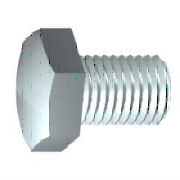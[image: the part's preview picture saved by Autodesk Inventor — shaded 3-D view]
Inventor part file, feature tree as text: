
AUTODESK INVENTOR PART (.ipt)
format: ipt  version: 2023 (Build 270158000, 158)  size: 218,112 bytes
history: native  units: mm
features: sketch x4, other x2, plane x1
ambient origin geometry x8: Origin, YZ Plane, XZ Plane, XY Plane, X Axis, Y Axis, Z Axis, Center Point
bodies: Solid1 (feature_tree)
feature tree (7):
  plane  "Work Plane1"
  sketch  "Sketch1"  dims[d6=0.6mm]
  sketch  "Sketch2"  dims[d7=11.63mm]
  sketch  "Sketch4"  dims[d9=135.0deg d10=8.0mm d11=25.0mm d13=90.0deg d14=22.0mm d15=0.0mm d16=0.6mm d17=2.0mm d18=45.0deg d19=13.0mm d20=15.011107mm d21=4.7mm d22=0.0mm d32=9.2mm d34=0.0mm d35=8.0mm d37=0.0mm d38=0.0mm d39=120.0deg d40=13.0mm d41=10.0mm d42=60.0deg d49=0.6mm d50=0.0mm]
  other  "Srf2"
  sketch  "Sketch3"  dims[d8=0.1mm]
  other  "Srf1"
